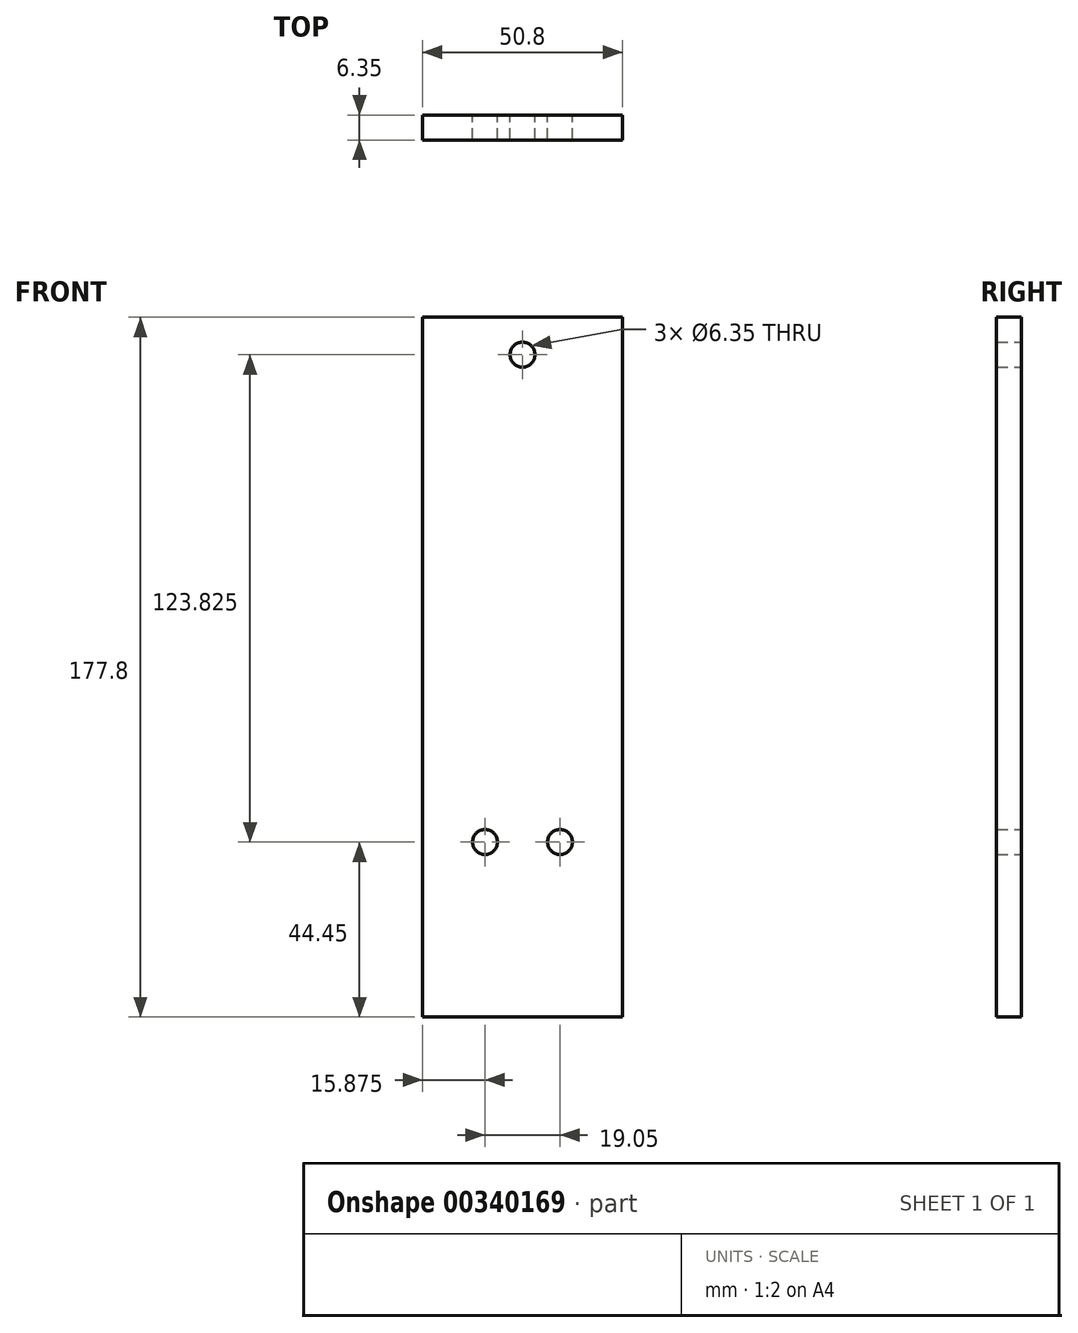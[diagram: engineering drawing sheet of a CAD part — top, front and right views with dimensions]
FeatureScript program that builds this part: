
annotation { "Feature Type Name" : "Feature", "Feature Type Description" : "" }
export const myFeature = defineFeature(function(context is Context, id is Id, definition is map)
    precondition{}
    {
        {
            var Q0;
            Q0=qCreatedBy(makeId("Front.planeOp"),FACE);
            var sketch = newSketch(context, id + "F0", { "sketchPlane" : qUnion([Q0])});
            skLineSegment(sketch, "E0.bottom", {"start": v(0, 0) * mm, "end": v(50.8, 0) * mm});
            skLineSegment(sketch, "E0.top", {"start": v(0, 177.8) * mm, "end": v(50.8, 177.8) * mm});
            skLineSegment(sketch, "E0.left", {"start": v(0, 0) * mm, "end": v(0, 177.8) * mm});
            skLineSegment(sketch, "E0.right", {"start": v(50.8, 0) * mm, "end": v(50.8, 177.8) * mm});
            skLineSegment(sketch, "E1", {"start": v(25.4, 177.8) * mm, "end": v(25.4, 44.45) * mm});
            skLineSegment(sketch, "E2", {"start": v(15.87, 44.45) * mm, "end": v(34.93, 44.45) * mm});
            skCircle(sketch, "E3", {"center": v(34.93, 44.45) * mm, "radius": 3.18 * mm});
            skCircle(sketch, "E4", {"center": v(15.87, 44.45) * mm, "radius": 3.18 * mm});
            skCircle(sketch, "E5", {"center": v(25.4, 168.28) * mm, "radius": 3.18 * mm});
            skSolve(sketch);
        }
        {
            var Q0;
            Q0 = qSketchRegion(id + "F0", true);
            extrude(context, id + "F1", {"entities" : qUnion([Q0]), "depth" : 6.35 * mm});
        }
    });
